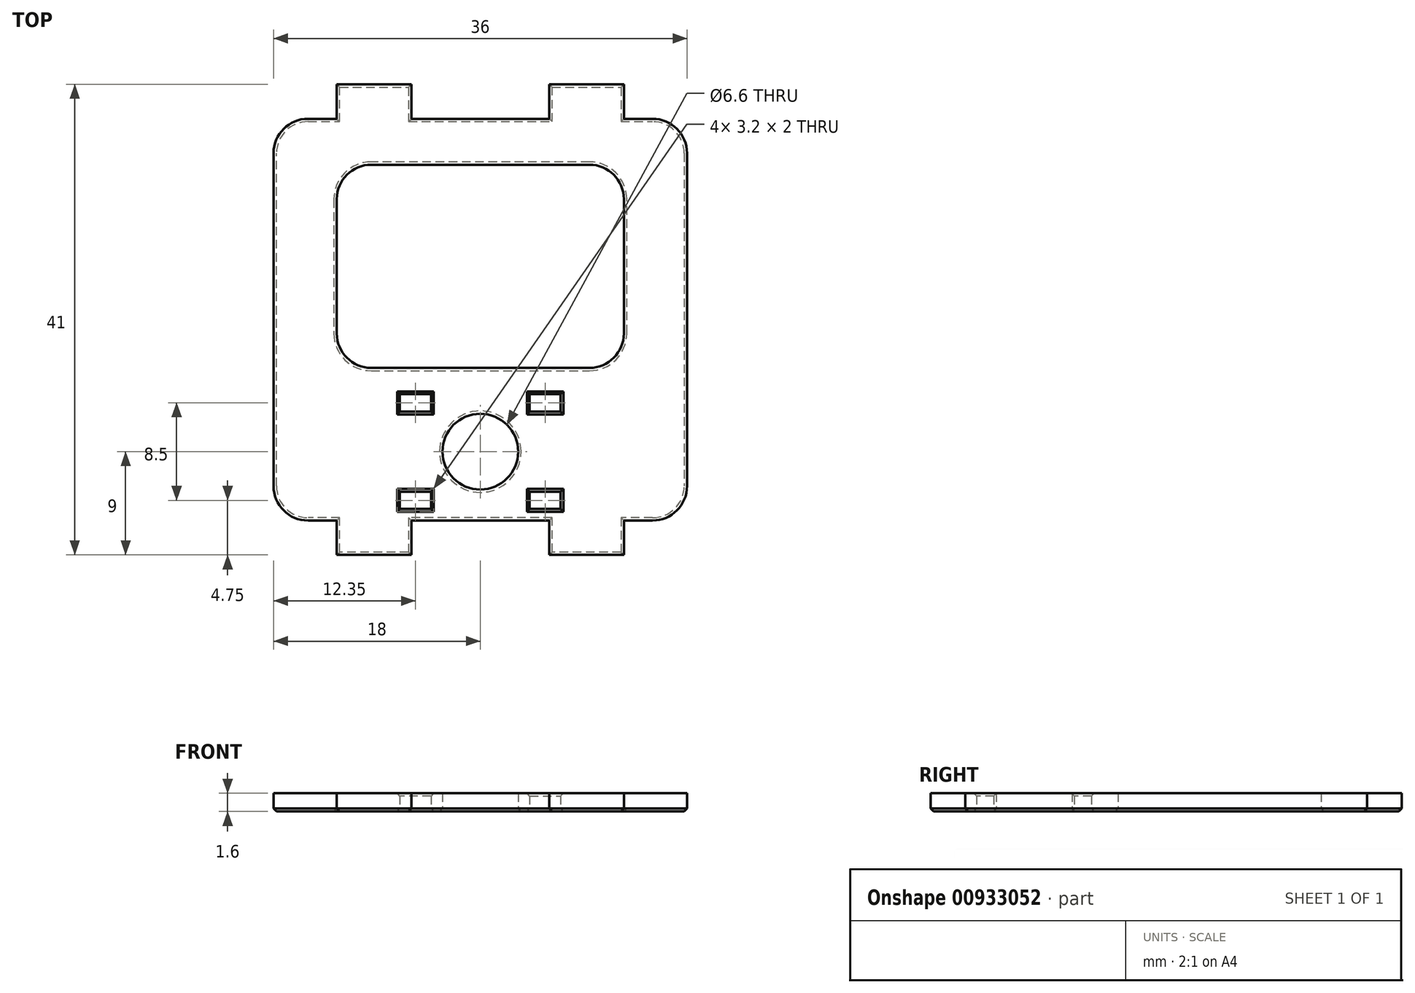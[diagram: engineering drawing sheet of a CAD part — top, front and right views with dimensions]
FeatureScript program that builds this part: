
annotation { "Feature Type Name" : "Feature", "Feature Type Description" : "" }
export const myFeature = defineFeature(function(context is Context, id is Id, definition is map)
    precondition{}
    {
        {
            var Q0;
            Q0=qCreatedBy(makeId("Top.planeOp"),FACE);
            var sketch = newSketch(context, id + "F0", { "sketchPlane" : qUnion([Q0])});
            skLineSegment(sketch, "E0.bottom", {"start": v(18, 17.5) * mm, "end": v(-18, 17.5) * mm});
            skLineSegment(sketch, "E0.top", {"start": v(18, -17.5) * mm, "end": v(-18, -17.5) * mm});
            skLineSegment(sketch, "E0.left", {"start": v(18, 17.5) * mm, "end": v(18, -17.5) * mm});
            skLineSegment(sketch, "E0.right", {"start": v(-18, 17.5) * mm, "end": v(-18, -17.5) * mm});
            skPoint(sketch, "E0.middle", {"position": v(0, 0) * mm});
            skLineSegment(sketch, "E1.bottom", {"start": v(-12.5, 17.5) * mm, "end": v(-6, 17.5) * mm});
            skLineSegment(sketch, "E1.top", {"start": v(-12.5, 20.5) * mm, "end": v(-6, 20.5) * mm});
            skLineSegment(sketch, "E1.left", {"start": v(-12.5, 17.5) * mm, "end": v(-12.5, 20.5) * mm});
            skLineSegment(sketch, "E1.right", {"start": v(-6, 17.5) * mm, "end": v(-6, 20.5) * mm});
            skLineSegment(sketch, "E2", {"start": v(0, 0) * mm, "end": v(0, 17.5) * mm, "construction": true});
            skLineSegment(sketch, "E3", {"start": v(0, 0) * mm, "end": v(-18, 0) * mm, "construction": true});
            skLineSegment(sketch, "E4.MirrorCS", {"start": v(6, 17.5) * mm, "end": v(6, 20.5) * mm});
            skLineSegment(sketch, "E5.MirrorCS", {"start": v(12.5, 20.5) * mm, "end": v(6, 20.5) * mm});
            skLineSegment(sketch, "E6.MirrorCS", {"start": v(12.5, 17.5) * mm, "end": v(12.5, 20.5) * mm});
            skLineSegment(sketch, "E7.MirrorCS", {"start": v(12.5, -17.5) * mm, "end": v(12.5, -20.5) * mm});
            skLineSegment(sketch, "E8.MirrorCS", {"start": v(12.5, -20.5) * mm, "end": v(6, -20.5) * mm});
            skLineSegment(sketch, "E9.MirrorCS", {"start": v(6, -17.5) * mm, "end": v(6, -20.5) * mm});
            skLineSegment(sketch, "E10.MirrorCS", {"start": v(-6, -17.5) * mm, "end": v(-6, -20.5) * mm});
            skLineSegment(sketch, "E11.MirrorCS", {"start": v(-12.5, -20.5) * mm, "end": v(-6, -20.5) * mm});
            skLineSegment(sketch, "E12.MirrorCS", {"start": v(-12.5, -17.5) * mm, "end": v(-12.5, -20.5) * mm});
            skCircle(sketch, "E13", {"center": v(0, -11.5) * mm, "radius": 3.3 * mm});
            skLineSegment(sketch, "E14.bottom", {"start": v(12.5, 13.5) * mm, "end": v(-12.5, 13.5) * mm});
            skLineSegment(sketch, "E14.top", {"start": v(12.5, -4.2) * mm, "end": v(-12.5, -4.2) * mm});
            skLineSegment(sketch, "E14.left", {"start": v(12.5, 13.5) * mm, "end": v(12.5, -4.2) * mm});
            skLineSegment(sketch, "E14.right", {"start": v(-12.5, 13.5) * mm, "end": v(-12.5, -4.2) * mm});
            skPoint(sketch, "E14.middle", {"position": v(0, 4.65) * mm});
            skLineSegment(sketch, "E15.bottom", {"start": v(-4.3, -8) * mm, "end": v(-7, -8) * mm});
            skLineSegment(sketch, "E15.top", {"start": v(-4.3, -6.5) * mm, "end": v(-7, -6.5) * mm});
            skLineSegment(sketch, "E15.left", {"start": v(-4.3, -8) * mm, "end": v(-4.3, -6.5) * mm});
            skLineSegment(sketch, "E15.right", {"start": v(-7, -8) * mm, "end": v(-7, -6.5) * mm});
            skLineSegment(sketch, "E16", {"start": v(0, -11.5) * mm, "end": v(-8.72, -11.5) * mm, "construction": true});
            skLineSegment(sketch, "E17.MirrorCS", {"start": v(-7, -15) * mm, "end": v(-7, -16.5) * mm});
            skLineSegment(sketch, "E18.MirrorCS", {"start": v(-4.3, -16.5) * mm, "end": v(-7, -16.5) * mm});
            skLineSegment(sketch, "E19.MirrorCS", {"start": v(-4.3, -15) * mm, "end": v(-4.3, -16.5) * mm});
            skLineSegment(sketch, "E20.MirrorCS", {"start": v(-4.3, -15) * mm, "end": v(-7, -15) * mm});
            skLineSegment(sketch, "E21.MirrorCS", {"start": v(4.3, -8) * mm, "end": v(4.3, -6.5) * mm});
            skLineSegment(sketch, "E22.MirrorCS", {"start": v(4.3, -6.5) * mm, "end": v(7, -6.5) * mm});
            skLineSegment(sketch, "E23.MirrorCS", {"start": v(7, -8) * mm, "end": v(7, -6.5) * mm});
            skLineSegment(sketch, "E24.MirrorCS", {"start": v(4.3, -8) * mm, "end": v(7, -8) * mm});
            skLineSegment(sketch, "E25.MirrorCS", {"start": v(4.3, -15) * mm, "end": v(7, -15) * mm});
            skLineSegment(sketch, "E26.MirrorCS", {"start": v(7, -15) * mm, "end": v(7, -16.5) * mm});
            skLineSegment(sketch, "E27.MirrorCS", {"start": v(4.3, -16.5) * mm, "end": v(7, -16.5) * mm});
            skLineSegment(sketch, "E28.MirrorCS", {"start": v(4.3, -15) * mm, "end": v(4.3, -16.5) * mm});
            skSolve(sketch);
        }
        {
            var Q0;
            Q0=qSketchRegion(id+"F0",true);
            extrude(context, id + "F1", {"entities" : qUnion([Q0]), "depth" : 1.6 * mm, "offsetDistance" : 25 * mm});
        }
        {
            var Q0;
            Q0=makeQuery(id+"F1.opExtrude","SWEPT_EDGE",EDGE,{"disambiguationData":[OSD([sQuery(id+"F0.wireOp",EDGE,"E0.bottom"),sQuery(id+"F0.wireOp",EDGE,"E0.right")])]});
            var Q1;
            Q1=makeQuery(id+"F1.opExtrude","SWEPT_EDGE",EDGE,{"disambiguationData":[OSD([sQuery(id+"F0.wireOp",EDGE,"E0.top"),sQuery(id+"F0.wireOp",EDGE,"E0.right")])]});
            var Q2;
            Q2=makeQuery(id+"F1.opExtrude","SWEPT_EDGE",EDGE,{"disambiguationData":[OSD([sQuery(id+"F0.wireOp",EDGE,"E0.top"),sQuery(id+"F0.wireOp",EDGE,"E0.left")])]});
            var Q3;
            Q3=makeQuery(id+"F1.opExtrude","SWEPT_EDGE",EDGE,{"disambiguationData":[OSD([sQuery(id+"F0.wireOp",EDGE,"E0.bottom"),sQuery(id+"F0.wireOp",EDGE,"E0.left")])]});
            var Q4;
            Q4=makeQuery(id+"F1.opExtrude","SWEPT_EDGE",EDGE,{"disambiguationData":[OSD([sQuery(id+"F0.wireOp",EDGE,"E14.top"),sQuery(id+"F0.wireOp",EDGE,"E14.right")])]});
            var Q5;
            Q5=makeQuery(id+"F1.opExtrude","SWEPT_EDGE",EDGE,{"disambiguationData":[OSD([sQuery(id+"F0.wireOp",EDGE,"E14.bottom"),sQuery(id+"F0.wireOp",EDGE,"E14.right")])]});
            var Q6;
            Q6=makeQuery(id+"F1.opExtrude","SWEPT_EDGE",EDGE,{"disambiguationData":[OSD([sQuery(id+"F0.wireOp",EDGE,"E14.bottom"),sQuery(id+"F0.wireOp",EDGE,"E14.left")])]});
            var Q7;
            Q7=makeQuery(id+"F1.opExtrude","SWEPT_EDGE",EDGE,{"disambiguationData":[OSD([sQuery(id+"F0.wireOp",EDGE,"E14.top"),sQuery(id+"F0.wireOp",EDGE,"E14.left")])]});
            fillet(context, id + "F2", {"entities" : qUnion([Q0, Q1, Q2, Q3, Q4, Q5, Q6, Q7]), "radius" : 3 * mm, "tangentPropagation" : true, "allowEdgeOverflow" : false});
        }
        {
            var Q0;
            Q0=makeQuery(id+"F1.opExtrude","CAP_FACE",FACE,{"disambiguationData":[OSD([sQuery(id+"F0.wireOp",EDGE,"E0.bottom"),sQuery(id+"F0.wireOp",EDGE,"E0.top"),sQuery(id+"F0.wireOp",EDGE,"E0.left"),sQuery(id+"F0.wireOp",EDGE,"E0.right"),sQuery(id+"F0.wireOp",EDGE,"E1.top"),sQuery(id+"F0.wireOp",EDGE,"E1.left"),sQuery(id+"F0.wireOp",EDGE,"E1.right"),sQuery(id+"F0.wireOp",EDGE,"E4.MirrorCS"),sQuery(id+"F0.wireOp",EDGE,"E5.MirrorCS"),sQuery(id+"F0.wireOp",EDGE,"E6.MirrorCS"),sQuery(id+"F0.wireOp",EDGE,"E7.MirrorCS"),sQuery(id+"F0.wireOp",EDGE,"E8.MirrorCS"),sQuery(id+"F0.wireOp",EDGE,"E9.MirrorCS"),sQuery(id+"F0.wireOp",EDGE,"E10.MirrorCS"),sQuery(id+"F0.wireOp",EDGE,"E11.MirrorCS"),sQuery(id+"F0.wireOp",EDGE,"E12.MirrorCS"),sQuery(id+"F0.wireOp",EDGE,"E13"),sQuery(id+"F0.wireOp",EDGE,"E14.bottom"),sQuery(id+"F0.wireOp",EDGE,"E14.top"),sQuery(id+"F0.wireOp",EDGE,"E14.left"),sQuery(id+"F0.wireOp",EDGE,"E14.right"),sQuery(id+"F0.wireOp",EDGE,"E15.bottom"),sQuery(id+"F0.wireOp",EDGE,"E15.top"),sQuery(id+"F0.wireOp",EDGE,"E15.left"),sQuery(id+"F0.wireOp",EDGE,"E15.right"),sQuery(id+"F0.wireOp",EDGE,"E17.MirrorCS"),sQuery(id+"F0.wireOp",EDGE,"E18.MirrorCS"),sQuery(id+"F0.wireOp",EDGE,"E19.MirrorCS"),sQuery(id+"F0.wireOp",EDGE,"E20.MirrorCS"),sQuery(id+"F0.wireOp",EDGE,"E21.MirrorCS"),sQuery(id+"F0.wireOp",EDGE,"E22.MirrorCS"),sQuery(id+"F0.wireOp",EDGE,"E23.MirrorCS"),sQuery(id+"F0.wireOp",EDGE,"E24.MirrorCS"),sQuery(id+"F0.wireOp",EDGE,"E25.MirrorCS"),sQuery(id+"F0.wireOp",EDGE,"E26.MirrorCS"),sQuery(id+"F0.wireOp",EDGE,"E27.MirrorCS"),sQuery(id+"F0.wireOp",EDGE,"E28.MirrorCS")])],"isStart":true});
            var Q1;
            Q1=makeQuery(id+"F1.opExtrude","CAP_EDGE",EDGE,{"disambiguationData":[OSD([sQuery(id+"F0.wireOp",EDGE,"E15.right")])],"isStart":false});
            var Q2;
            Q2=makeQuery(id+"F1.opExtrude","CAP_EDGE",EDGE,{"disambiguationData":[OSD([sQuery(id+"F0.wireOp",EDGE,"E15.top")])],"isStart":false});
            var Q3;
            Q3=makeQuery(id+"F1.opExtrude","CAP_EDGE",EDGE,{"disambiguationData":[OSD([sQuery(id+"F0.wireOp",EDGE,"E15.left")])],"isStart":false});
            var Q4;
            Q4=makeQuery(id+"F1.opExtrude","CAP_EDGE",EDGE,{"disambiguationData":[OSD([sQuery(id+"F0.wireOp",EDGE,"E15.bottom")])],"isStart":false});
            var Q5;
            Q5=makeQuery(id+"F1.opExtrude","CAP_EDGE",EDGE,{"disambiguationData":[OSD([sQuery(id+"F0.wireOp",EDGE,"E20.MirrorCS")])],"isStart":false});
            var Q6;
            Q6=makeQuery(id+"F1.opExtrude","CAP_EDGE",EDGE,{"disambiguationData":[OSD([sQuery(id+"F0.wireOp",EDGE,"E17.MirrorCS")])],"isStart":false});
            var Q7;
            Q7=makeQuery(id+"F1.opExtrude","CAP_EDGE",EDGE,{"disambiguationData":[OSD([sQuery(id+"F0.wireOp",EDGE,"E18.MirrorCS")])],"isStart":false});
            var Q8;
            Q8=makeQuery(id+"F1.opExtrude","CAP_EDGE",EDGE,{"disambiguationData":[OSD([sQuery(id+"F0.wireOp",EDGE,"E19.MirrorCS")])],"isStart":false});
            var Q9;
            Q9=makeQuery(id+"F1.opExtrude","CAP_EDGE",EDGE,{"disambiguationData":[OSD([sQuery(id+"F0.wireOp",EDGE,"E21.MirrorCS")])],"isStart":false});
            var Q10;
            Q10=makeQuery(id+"F1.opExtrude","CAP_EDGE",EDGE,{"disambiguationData":[OSD([sQuery(id+"F0.wireOp",EDGE,"E22.MirrorCS")])],"isStart":false});
            var Q11;
            Q11=makeQuery(id+"F1.opExtrude","CAP_EDGE",EDGE,{"disambiguationData":[OSD([sQuery(id+"F0.wireOp",EDGE,"E23.MirrorCS")])],"isStart":false});
            var Q12;
            Q12=makeQuery(id+"F1.opExtrude","CAP_EDGE",EDGE,{"disambiguationData":[OSD([sQuery(id+"F0.wireOp",EDGE,"E24.MirrorCS")])],"isStart":false});
            var Q13;
            Q13=makeQuery(id+"F1.opExtrude","CAP_EDGE",EDGE,{"disambiguationData":[OSD([sQuery(id+"F0.wireOp",EDGE,"E25.MirrorCS")])],"isStart":false});
            var Q14;
            Q14=makeQuery(id+"F1.opExtrude","CAP_EDGE",EDGE,{"disambiguationData":[OSD([sQuery(id+"F0.wireOp",EDGE,"E28.MirrorCS")])],"isStart":false});
            var Q15;
            Q15=makeQuery(id+"F1.opExtrude","CAP_EDGE",EDGE,{"disambiguationData":[OSD([sQuery(id+"F0.wireOp",EDGE,"E27.MirrorCS")])],"isStart":false});
            var Q16;
            Q16=makeQuery(id+"F1.opExtrude","CAP_EDGE",EDGE,{"disambiguationData":[OSD([sQuery(id+"F0.wireOp",EDGE,"E26.MirrorCS")])],"isStart":false});
            chamfer(context, id + "F3", {"entities" : qUnion([Q0, Q1, Q2, Q3, Q4, Q5, Q6, Q7, Q8, Q9, Q10, Q11, Q12, Q13, Q14, Q15, Q16]), "width" : 0.25 * mm, "tangentPropagation" : true});
        }
    });
